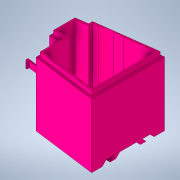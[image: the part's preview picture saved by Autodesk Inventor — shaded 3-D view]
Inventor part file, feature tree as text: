
AUTODESK INVENTOR PART (.ipt)
format: ipt  version: 2020 (Build 240168000, 168)  size: 299,520 bytes
history: native  units: mm
features: extrude x9, sketch x9, reference x3, other x3, chamfer x1, plane x1, mirror x1, projected_geometry x1
ambient origin geometry x8: Origin, YZ Plane, XZ Plane, XY Plane, X Axis, Y Axis, Z Axis, Center Point
bodies: Solid1 (feature_tree)
feature tree (28):
  extrude  "Extrusion1"  Depth=5.0mm TaperAngle=0.0deg
  extrude  "Extrusion2"  Depth=5.0mm
  extrude  "Extrusion3"  Depth=5.0mm
  extrude  "Extrusion4"  Depth=5.0mm
  extrude  "Extrusion5"  Depth=5.0mm
  extrude  "Extrusion6"  Depth=5.0mm
  extrude  "Extrusion7"  Depth=70.0mm TaperAngle=0.0deg
  chamfer  "Chamfer1"  Distance=2.35mm
  plane  "Work Plane1"
  mirror  "Mirror1"
  extrude  "Extrusion8"  Depth=2.5mm
  extrude  "Extrusion9"  Depth=2.35mm
  sketch  "Sketch1"  dims[d0=5.0mm d1=0.0mm d2=5.0mm d3=0.0mm]
  reference  "Reference1"
  reference  "Reference2"
  reference  "Reference3"
  sketch  "Sketch3"  dims[d4=0.0mm d5=0.0mm d6=5.0mm]
  sketch  "Sketch4"  dims[d7=5.0mm d8=5.0mm]
  projected_geometry  "Projected Loop1"
  sketch  "Sketch5"  dims[d9=5.0mm d10=5.0mm]
  sketch  "Sketch6"  dims[d11=5.0mm d12=5.0mm]
  sketch  "Sketch7"  dims[d13=5.0mm d14=5.0mm]
  sketch  "Sketch8"  dims[d15=5.0mm d17=70.0mm d18=0.0mm]
  sketch  "Sketch9"  dims[d19=2.35mm]
  sketch  "Sketch10"  dims[d20=2.35mm d21=2.35mm d22=2.5mm d23=2.35mm d24=2.35mm d25=2.35mm d27=6.0mm d28=0.0mm d29=10.0mm d30=55.0mm d31=4.0mm d32=0.0mm d33=10.0mm d34=1.2mm d37=1.0mm d38=1.0mm d39=15.0mm d40=2.0mm d41=0.0mm d42=0.0mm d43=3.0mm d44=3.0mm d45=0.0mm d46=2.0mm d47=2.0mm d48=45.0deg d49=5.8mm d50=10.0mm d51=0.0mm d52=3.0mm d54=30.0mm d55=10.0mm d56=0.0mm d57=49.0mm]
  parser-record x1  (decoder bookkeeping rows leaked as tree rows — omitted from the tree; the rows remain in map.json)
  other  "steering_queens_pair.iam"
  other  "hull_main:1"
note: 1 file-system path scrubbed to <path> (originals preserved in map.json)
